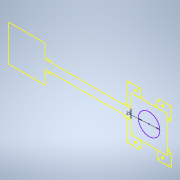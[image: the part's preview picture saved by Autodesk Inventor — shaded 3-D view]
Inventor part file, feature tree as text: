
AUTODESK INVENTOR PART (.ipt)
format: ipt  version: 2022 (Build 260153000, 153)  size: 109,568 bytes
history: native  units: mm
features: reference x5, other x3, sketch x1
ambient origin geometry x8: Origin, YZ Plane, XZ Plane, XY Plane, X Axis, Y Axis, Z Axis, Center Point
feature tree (9):
  sketch  "Sketch1"  dims[d0=25.0mm]
  reference  "Reference1"
  reference  "Reference2"
  reference  "Reference3"
  reference  "Reference4"
  reference  "Reference5"
  other  "<userpath>\OneDrive\Namizje\school\3. letnik\ZOPp\laserski merilnik\3d model\Assembly1.iam"
  other  "Assembly1.iam"
  other  "Hold of motors:1"
